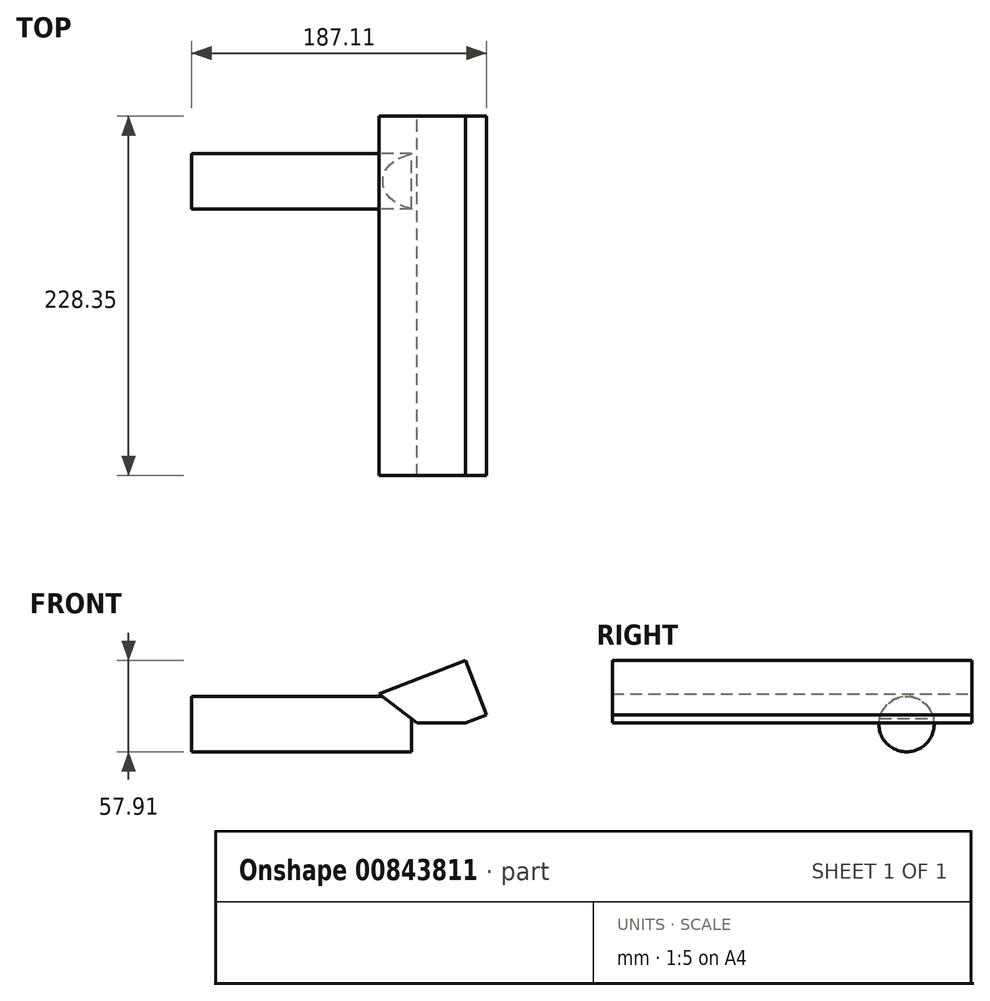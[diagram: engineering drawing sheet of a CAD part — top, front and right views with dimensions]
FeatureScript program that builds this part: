
annotation { "Feature Type Name" : "Feature", "Feature Type Description" : "" }
export const myFeature = defineFeature(function(context is Context, id is Id, definition is map)
    precondition{}
    {
        {
            var Q0;
            Q0=qCreatedBy(makeId("Front.planeOp"),FACE);
            var sketch = newSketch(context, id + "F0", { "sketchPlane" : qUnion([Q0])});
            skLineSegment(sketch, "E0", {"start": v(119, 67.85) * mm, "end": v(173.9, 88.87) * mm});
            skLineSegment(sketch, "E1", {"start": v(173.9, 88.87) * mm, "end": v(187.11, 54.4) * mm});
            skLineSegment(sketch, "E2", {"start": v(187.11, 54.4) * mm, "end": v(173.9, 49.33) * mm});
            skLineSegment(sketch, "E3", {"start": v(173.9, 49.33) * mm, "end": v(143.22, 49.33) * mm});
            skLineSegment(sketch, "E4", {"start": v(143.22, 49.33) * mm, "end": v(119, 67.85) * mm});
            skSolve(sketch);
        }
        {
            var Q0;
            Q0=qCreatedBy(makeId("Right.planeOp"),FACE);
            var sketch = newSketch(context, id + "F1", { "sketchPlane" : qUnion([Q0])});
            skCircle(sketch, "E5", {"center": v(-41.43, 48.55) * mm, "radius": 17.59 * mm});
            skSolve(sketch);
        }
        {
            var Q0;
            Q0=makeQuery(id+"F1.imprint","IMPRINT",FACE,{"disambiguationData":[TD([[makeQuery(id+"F1.imprint","IMPRINT",EDGE,{"derivedFrom":sQuery(id+"F1.wireOp",EDGE,"E5")}),1.0]])]});
            extrude(context, id + "F2", {"entities" : qUnion([Q0]), "depth" : 139.7 * mm, "offsetDistance" : 25.4 * mm});
        }
        {
            var Q0;
            Q0=makeQuery(id+"F0.imprint","IMPRINT",FACE,{"disambiguationData":[TD([[makeQuery(id+"F0.imprint","IMPRINT",EDGE,{"derivedFrom":sQuery(id+"F0.wireOp",EDGE,"E0")}),-1.0]])]});
            extrude(context, id + "F3", {"entities" : qUnion([Q0]), "operationType" : NewBodyOperationType.ADD, "depth" : 228.35 * mm, "offsetDistance" : 25.4 * mm});
        }
    });
